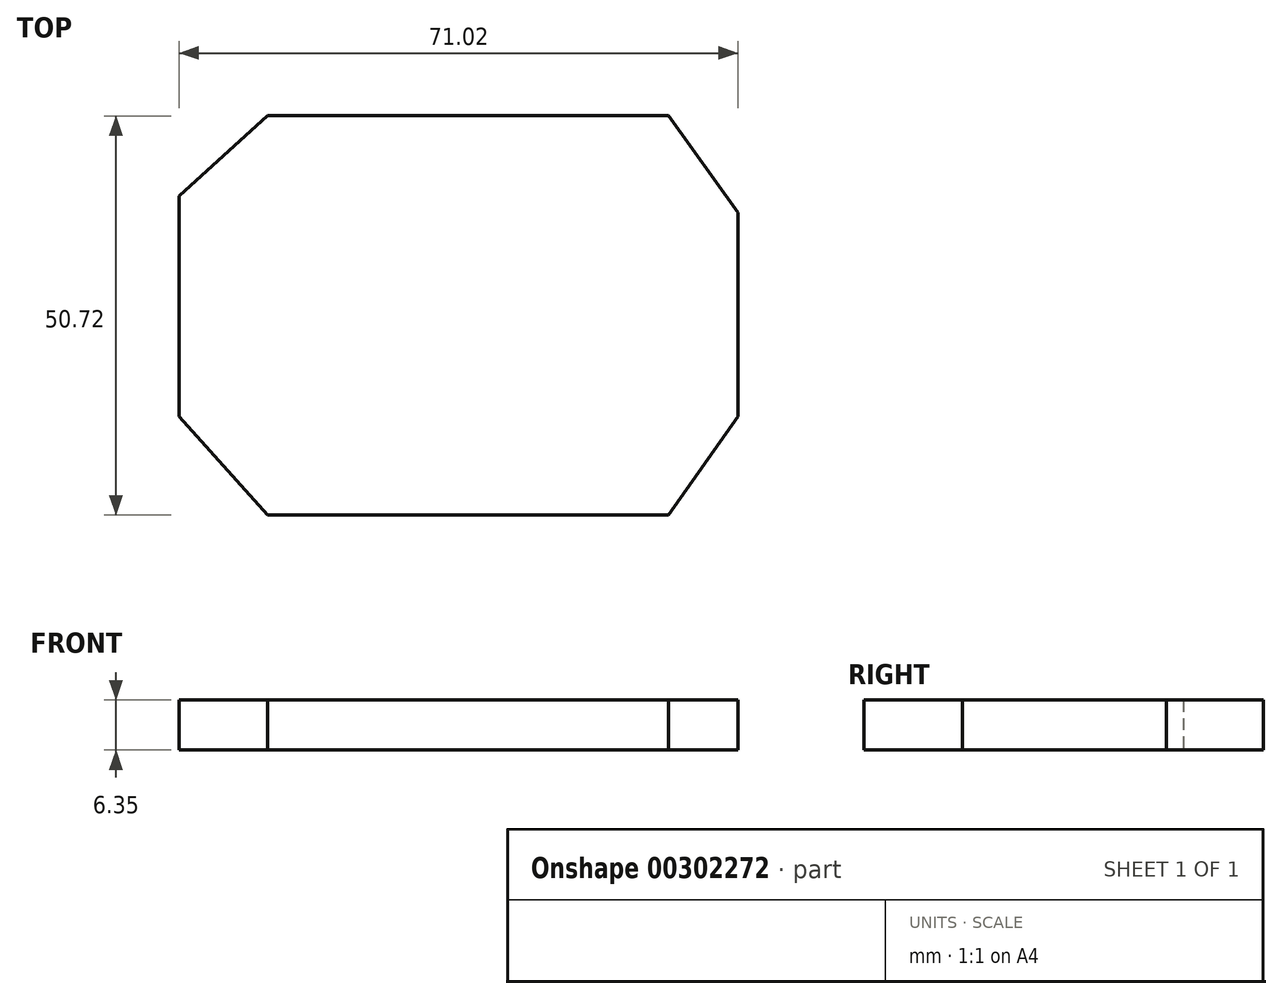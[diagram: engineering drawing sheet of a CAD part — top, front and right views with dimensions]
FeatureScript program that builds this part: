
annotation { "Feature Type Name" : "Feature", "Feature Type Description" : "" }
export const myFeature = defineFeature(function(context is Context, id is Id, definition is map)
    precondition{}
    {
        {
            var Q0;
            Q0=qCreatedBy(makeId("Top.planeOp"),FACE);
            var sketch = newSketch(context, id + "F0", { "sketchPlane" : qUnion([Q0])});
            skLineSegment(sketch, "E0", {"start": v(-44.8, 14.17) * mm, "end": v(-44.8, -13.87) * mm});
            skLineSegment(sketch, "E1", {"start": v(-44.8, -13.87) * mm, "end": v(-33.53, -26.37) * mm});
            skLineSegment(sketch, "E2", {"start": v(-33.53, -26.37) * mm, "end": v(17.37, -26.37) * mm});
            skLineSegment(sketch, "E3", {"start": v(17.37, -26.37) * mm, "end": v(26.21, -13.87) * mm});
            skLineSegment(sketch, "E4", {"start": v(26.21, -13.87) * mm, "end": v(26.21, 12.04) * mm});
            skLineSegment(sketch, "E5", {"start": v(-44.8, 14.17) * mm, "end": v(-33.53, 24.35) * mm});
            skLineSegment(sketch, "E6", {"start": v(-33.53, 24.35) * mm, "end": v(17.37, 24.35) * mm});
            skLineSegment(sketch, "E7", {"start": v(17.37, 24.35) * mm, "end": v(26.21, 12.04) * mm});
            skSolve(sketch);
        }
        {
            var Q0;
            Q0=makeQuery(id+"F0.imprint","IMPRINT",FACE,{"disambiguationData":[TD([[makeQuery(id+"F0.imprint","IMPRINT",EDGE,{"derivedFrom":sQuery(id+"F0.wireOp",EDGE,"E0")}),1.0]])]});
            extrude(context, id + "F1", {"entities" : qUnion([Q0]), "depth" : 6.35 * mm});
        }
    });
